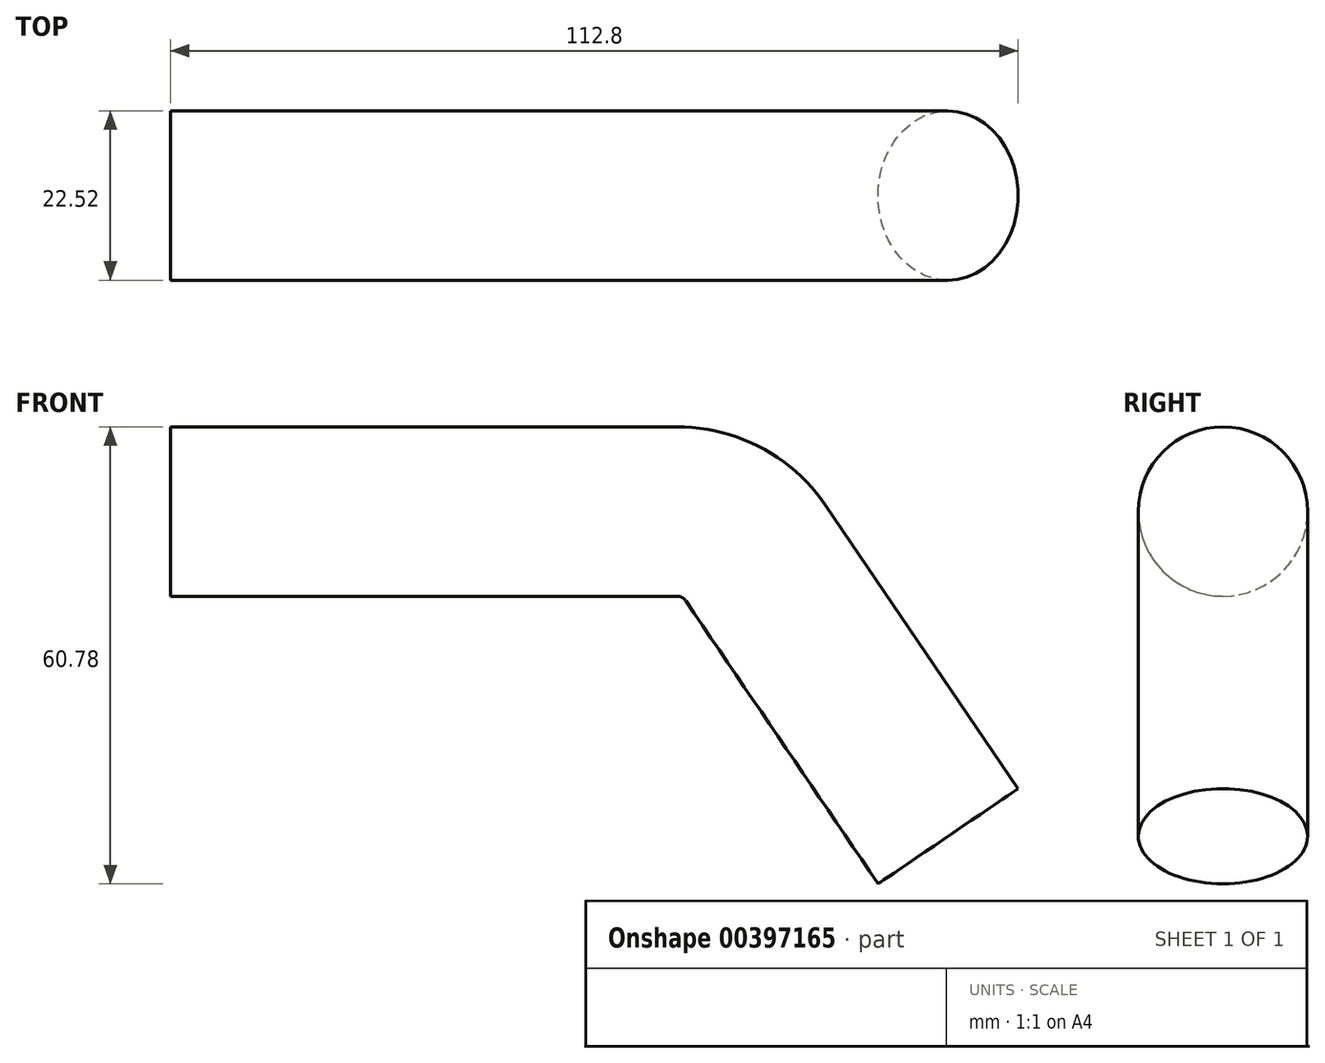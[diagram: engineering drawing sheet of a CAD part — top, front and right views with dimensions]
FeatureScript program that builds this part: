
annotation { "Feature Type Name" : "Feature", "Feature Type Description" : "" }
export const myFeature = defineFeature(function(context is Context, id is Id, definition is map)
    precondition{}
    {
        {
            var Q0;
            Q0=qCreatedBy(makeId("Front.planeOp"),FACE);
            var sketch = newSketch(context, id + "F0", { "sketchPlane" : qUnion([Q0])});
            skLineSegment(sketch, "E0", {"start": v(0, 0) * mm, "end": v(67.4, 0) * mm});
            skLineSegment(sketch, "E1", {"start": v(77.9, -5.56) * mm, "end": v(103.49, -43.19) * mm});
            skPoint(sketch, "E2.visualSharp", {"position": v(74.12, 0) * mm});
            skArc(sketch, "E2.filletArc", {"start": v(77.9, -5.56) * mm, "mid": v(73.34, -1.48) * mm, "end": v(67.4, 0) * mm});
            skSolve(sketch);
        }
        {
            var Q0;
            Q0=qCreatedBy(makeId("Right.planeOp"),FACE);
            var sketch = newSketch(context, id + "F1", { "sketchPlane" : qUnion([Q0])});
            skCircle(sketch, "E3", {"center": v(0, 0) * mm, "radius": 11.26 * mm});
            skSolve(sketch);
        }
        {
            var Q0;
            Q0=makeQuery(id+"F1.imprint","IMPRINT",FACE,{"disambiguationData":[TD([[makeQuery(id+"F1.imprint","IMPRINT",EDGE,{"derivedFrom":sQuery(id+"F1.wireOp",EDGE,"E3")}),1.0]])]});
            var Q1;
            Q1=sQuery(id+"F0.wireOp",EDGE,"E0");
            var Q2;
            Q2=sQuery(id+"F0.wireOp",EDGE,"E2.filletArc");
            var Q3;
            Q3=sQuery(id+"F0.wireOp",EDGE,"E1");
            sweep(context, id + "F2", {"profiles" : qUnion([Q0]), "path" : qUnion([Q1, Q2, Q3])});
        }
    });
